# Revit family: Lavatory-Sink-Excel_Dryer-D13-90in-Triple_Basin
name_source: partatom
category: Specialty Equipment
revit_build: Autodesk Revit 2018 (Build: 20190510_1515(x64)
units: mm (PartAtom-declared; Revit-internal decimal feet)

## family parameters
Cut with Voids When Loaded = No
Host = Face
OmniClass Number = 23.45.05.14.14
OmniClass Title = Sinks/Lavatories
Part Type = Normal
Room Calculation Point = No
Round Connector Dimension = Use Diameter
Shared = No

## types (12) — shared parameters
Apparent Load = 500 VA
Cabinet Finish = Surface - Excel Dryer - D13 - Polar White
Cold Water Connection Diameter = 0' - 0 1/2"
Cost Information = https://www.d13group.com
Counter Finish = Solid Surface - DuPont - Corian Solid Surface - Glacier White 1/2" (12mm)
Default Elevation = 0' - 0"
Depth = 2' - 0"
Description = D13 - 90" Basin
Drain Connection Diameter = 0' - 1"
Fixture Finish = Metal - Excel Dryer - Chrome - Polished
Frequency = 60 Hz
Full Trough Sink = Yes
Height = 2' - 10"
Hot Water Connection Diameter = 0' - 0 1/2"
Individual Cast Sink = No
Installation URL = https://www.d13group.com
Manufacturer = D|13 Group
Model = D13-GRA-INFINITY-90
Number of Poles = 1
Panel Finish = Solid Surface - DuPont - Corian Solid Surface - Glacier White 1/2" (12mm)
Phase = 1
Power Factor = 1
Product Documentation Link = https://www.d13group.com
Product Page URL = https://www.d13group.com
Splash Guard Finish = Solid Surface - DuPont - Corian Solid Surface - Glacier White 1/2" (12mm)
URL = https://www.d13group.com
Version = 2018 - v1.0b
Voltage = 120 V
Warranty URL = https://www.d13group.com
Watts = 500 W

## per-type parameters (varying)
| type | Faucet | Sink Finish | Soap Dispenser |
| 90" - Gradient Trough with Infinity Drain - Condor 1010-E Faucet - Stern Green Soap Dispenser | Faucet-Bathroom-Excel_Dryer-Stern_Condor-1010E : Stern Condor 1010-E Faucet | Solid Surface - DuPont - Corian Solid Surface - Glacier White 1/2" (12mm) | Bath_Accessory-Excel_Dryer-Stern-Soap_Dispenser-Green_Electronic-1.6E : Stern Green Liquid Soap Dispenser |
| 90" - Gradient Trough with Infinity Drain - (CUSTOM) Faucet - (CUSTOM) Soap Dispenser | Excel_Dryer-Faucet : Faucet | Solid Surface - DuPont - Corian Solid Surface - Glacier White 1/2" (12mm) | Excel_Dryer-Soap_Disp : Soap_Disp |
| 90" - Gradient Trough with Infinity Drain - Stern Elite LE Faucet - Stern Elite E Soap Dispenser | Faucet-Bathroom-Excel_Dryer-Stern-Touchless_Stern_Elite_LE : Stern Elite LE Faucet | Solid Surface - DuPont - Corian Solid Surface - Glacier White 1/2" (12mm) | Bath_Accessory-Excel_Dryer-Stern-Soap_Dispenser-Touchless_Stern_Elite : Stern Elite E Liquid Soap Dispenser |
| 90" - Gradient Trough with Infinity Drain - Stern Extreme HLE Faucet - Stern Extreme E Soap Dispenser | Faucet-Bathroom-Excel_Dryer-Stern-Touchless_Stern_Extreme-LF : Faucet Stern Extreme LFE | Solid Surface - DuPont - Corian Solid Surface - Glacier White 1/2" (12mm) | Bath_Accessory-Excel_Dryer-Stern-Soap_Dispenser-Extreme : Stern Extreme E Liquid Soap Dispenser |
| 90" - Gradient Trough with Infinity Drain - Trendy LE Faucet - Stern Trendy E Soap Dispenser | Faucet-Bathroom-Excel_Dryer-Stern-Touchless-Trendy-Mixer-1000-L : Trendy LE Faucet | Solid Surface - DuPont - Corian Solid Surface - Glacier White 1/2" (12mm) | Bath_Accessory-Excel_Dryer-Stern-Soap_Dispenser-Trendy : Stern Trendy E Liquid Soap Dispenser |
| 90" - Gradient Trough with Infinity Drain - Zurn Faucet - Zurn Soap Dispenser | Faucet_Bathroom-Excel_Dryer-Zurn-Battery_Powered-Z6953-XL : Zurn Camaya Water Faucet | Solid Surface - DuPont - Corian Solid Surface - Glacier White 1/2" (12mm) | Bath_Accessory-Excel_Dryer-Zurn-Soap_Dispenser-Z6953-SD : Zurn Liquid Soap Dispenser |
| 90" - Basin Undermount Sink with Pivot Drain Cover - Condor 1010-E Faucet - Stern Green Soap Dispenser | Faucet-Bathroom-Excel_Dryer-Stern_Condor-1010E : Stern Condor 1010-E Faucet | Surface - Excel Dryer - D13 - Polar White | Bath_Accessory-Excel_Dryer-Stern-Soap_Dispenser-Green_Electronic-1.6E : Stern Green Liquid Soap Dispenser |
| 90" - Basin Undermount Sink with Pivot Drain Cover - (CUSTOM) Faucet - (CUSTOM) Soap Dispenser | Excel_Dryer-Faucet : Faucet | Surface - Excel Dryer - D13 - Polar White | Excel_Dryer-Soap_Disp : Soap_Disp |
| 90" - Basin Undermount Sink with Pivot Drain Cover - Stern Elite LE Faucet - Stern Elite E Soap Dispenser | Faucet-Bathroom-Excel_Dryer-Stern-Touchless-Trendy-Mixer-1000-L : Trendy LE Faucet | Surface - Excel Dryer - D13 - Polar White | Bath_Accessory-Excel_Dryer-Stern-Soap_Dispenser-Touchless_Stern_Elite : Stern Elite E Liquid Soap Dispenser |
| 90" - Basin Undermount Sink with Pivot Drain Cover - Stern Swan Fucet - Stern Swan E Soap Dispenser | Faucet-Bathroom-Excel_Dryer-Stern-Touchless-Swan_Mixer-1010E : Stern Swan Fucet | Surface - Excel Dryer - D13 - Polar White | Bath_Accessory-Excel_Dryer-Stern-Soap_Dispenser-Swan-Mixer 1010E : Stern Swan E Liquid Dispenser |
| 90" - Basin Undermount Sink with Pivot Drain Cover - Trendy LE Faucet - Stern Trendy E Soap Dispenser | Faucet-Bathroom-Excel_Dryer-Stern-Touchless-Trendy-Mixer-1000-L : Trendy LE Faucet | Surface - Excel Dryer - D13 - Polar White | Bath_Accessory-Excel_Dryer-Stern-Soap_Dispenser-Trendy : Stern Trendy E Liquid Soap Dispenser |
| 90" - Basin Undermount Sink with Pivot Drain Cover - Zurn Faucet - Zurn Soap Dispenser | Faucet_Bathroom-Excel_Dryer-Zurn-Battery_Powered-Z6953-XL : Zurn Camaya Water Faucet | Surface - Excel Dryer - D13 - Polar White | Bath_Accessory-Excel_Dryer-Zurn-Soap_Dispenser-Z6953-SD : Zurn Liquid Soap Dispenser |

note: column(s) folded — value = type name in every type: Product Name

## geometry (parser evidence)
native form markers: Sweep x50
no freeform markers — native parametric forms only
